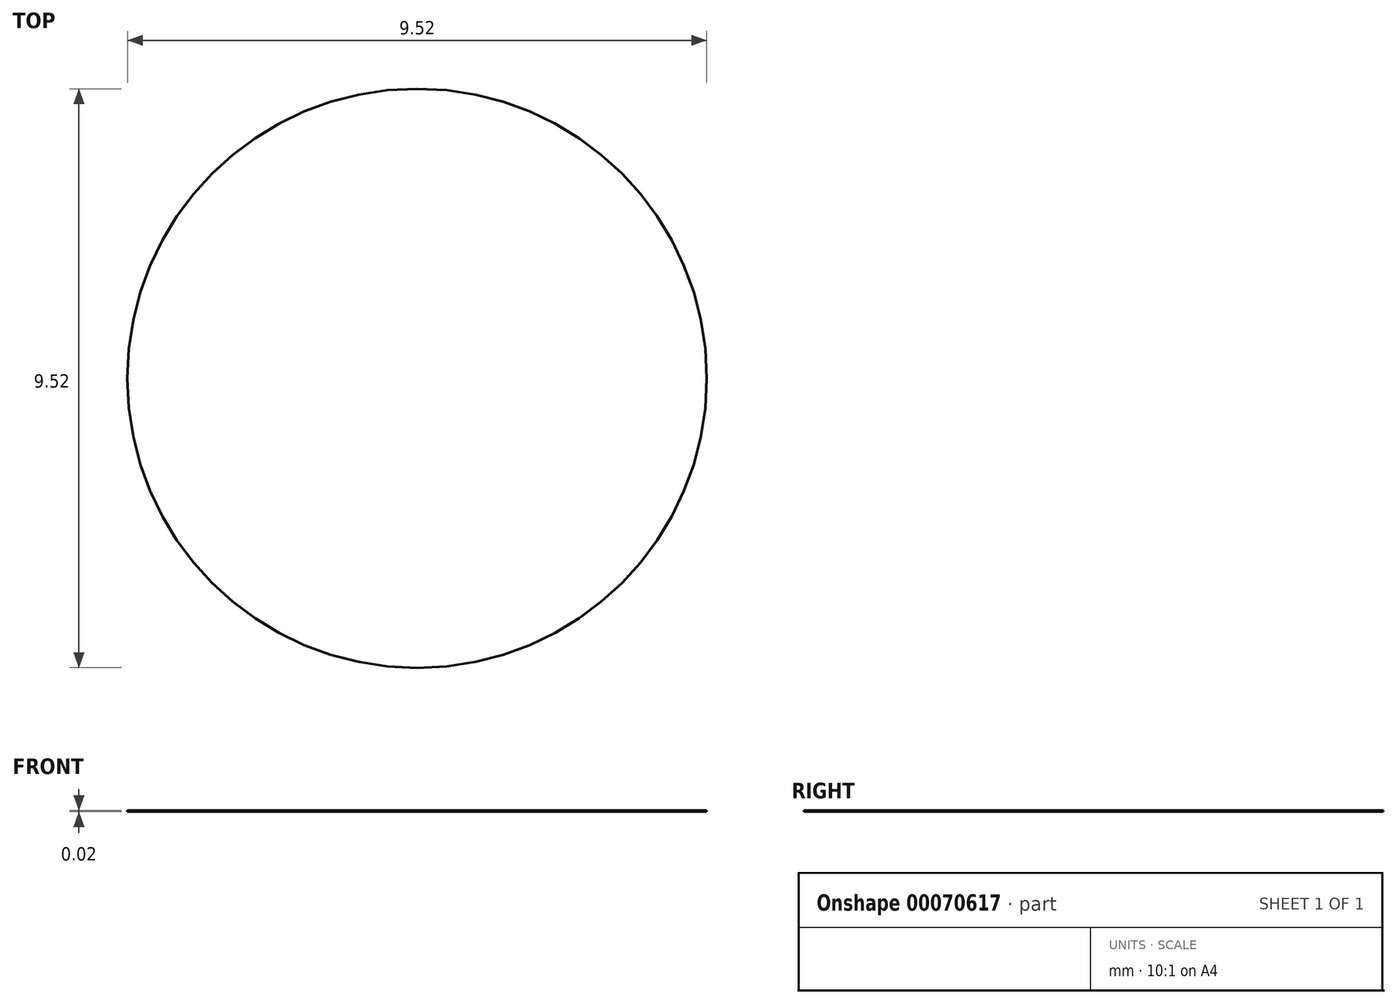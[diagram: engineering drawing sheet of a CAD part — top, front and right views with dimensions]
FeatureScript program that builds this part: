
annotation { "Feature Type Name" : "Feature", "Feature Type Description" : "" }
export const myFeature = defineFeature(function(context is Context, id is Id, definition is map)
    precondition{}
    {
        {
            var Q0;
            Q0=qCreatedBy(makeId("Top.planeOp"),FACE);
            var sketch = newSketch(context, id + "F0", { "sketchPlane" : qUnion([Q0])});
            skCircle(sketch, "E0", {"center": v(0, 0) * mm, "radius": 4.76 * mm});
            skSolve(sketch);
        }
        {
            var Q0;
            Q0=makeQuery(id+"F0.imprint","IMPRINT",FACE,{"disambiguationData":[TD([[makeQuery(id+"F0.imprint","IMPRINT",EDGE,{"derivedFrom":sQuery(id+"F0.wireOp",EDGE,"E0")}),1.0]])]});
            extrude(context, id + "F1", {"entities" : qUnion([Q0]), "depth" : 15 / 812.8 * mm});
        }
    });
